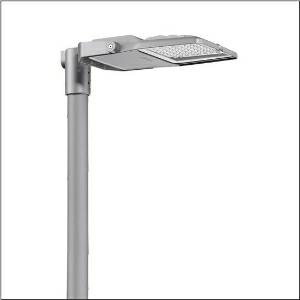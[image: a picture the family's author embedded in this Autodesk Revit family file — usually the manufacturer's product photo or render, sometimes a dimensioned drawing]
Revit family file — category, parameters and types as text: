
# Revit family: floodlight_fl_21_iq_mini___pl43_5xa7772b4a3a_1e53
name_source: partatom
category: Lighting Fixtures
units: mm (PartAtom-declared; Revit-internal decimal feet)

## family parameters
Cut with Voids When Loaded = No
Host = Face
Light Source = No
Part Type = Normal
Room Calculation Point = No
Round Connector Dimension = Use Diameter
Shared = No

## types (1)
- --- (1 x LED, 6660 lm, 45.5 W, 4000K)
    Apparent Load = 46 VA
    CIE Flux Codes = 27 78 99 100 100
    Color Rendering = 70
    Color Temperature = 4000K
    Default Elevation = 1800 mm
    Description = Floodlight FL 21 iQ mini, floodlight, primary light control with lens, of PMMA, primary optical cover: protective disc, of toughened safety glass, transparent, light distribution: PL43, light emission: direct distribution, installation type: surface-mounted, LED, High Power LED, rated luminous flux: 6.660lm, luminous efficacy: 146lm/W, light colour: 740, colour temperature: 4000K, control gear: iQ Street-Remote/DALI, control: Auto-Match, Temp-Guard, Night-Set, Smart-Wire, Desk-Remote (wireless, voltage-free reading and setting of iQ features in the workshop via application-optimized NFC function/RFID function), optimised constant luminous flux control (CLO 2.0), Light-Fading, Lumen-Switch, with terminal, 6-pole, mains connection: 220..240V, AC, 50/60Hz, start of lifetime: 46W, end of service life: 48W, reduction: 22W, luminaire housing, of diecast aluminium, powder-coated, Siteco® metallic grey (DB 702S), corrosivity category C5 mid according to DIN EN ISO 12944, suitable for swimming pools, chlorine-resistant, sealing non-destructively replaceable, please order mast flange separately, mast bracket, of steel, galvanised, powder-coated, protection rating (complete): IP66, insulation class (complete): insulation class II (safety insulation), certification: CE, ENEC, VDE, protection symbol: D, impact resistance: IK08, permissible operating ambient temperature: -40..+40°C, permissible operating ambient temperature for outdoor applications: -40..+50°C, standard: DIN EN 12944, LABS conformity tested according to VDMA 24364:2018-05, packaging unit: 1 piece

Light Distribution: PL43
    Height = 70 mm
    Lamp = 1 x LED
    Lamp Light Flux = 6660 lm
    Lamp Power = 45.5 W
    Lamp count = 1
    Length = 485 mm
    Luminous efficacy = 146 lm/W
    Manufacturer = Siteco
    ModVariant = No
    Model = 5XA7772B4A3A
    Number of Poles = 1
    OnlyDefault = Yes
    Power Factor = 1
    Product Name = Floodlight FL 21 iQ mini | PL43
    Product group = floodlight | pylon annexe
    ProductGroupID = 6201
    Protection Class = Protection class II
    Protection Degree = IP 66
    RLX_Detail_Level = 1
    RLX_Emergency_Light_Flux = 0 lm
    RLX_Emergency_Type = 0
    RLX_Emergency_Type_DB = No
    RlxData = <blob elided: 101233 chars, md5=3925a582>
    Socket = socket
    Standby Power = 0 W
    System Light Flux = 6660 lm
    System Power = 46 W
    Type Comments = factory setting: luminous flux: 100 % | dim-lin: 254 | 463 mA
    Type Image = l_1007125.jpg
    URL = http://relux.com
    VarID = @adj_184131
    Voltage = 0 V
    Weight = 0.00 kg
    Width = 337 mm

## geometry (parser evidence)
native form markers: Blend x4, Sweep x12
no freeform markers — native parametric forms only
